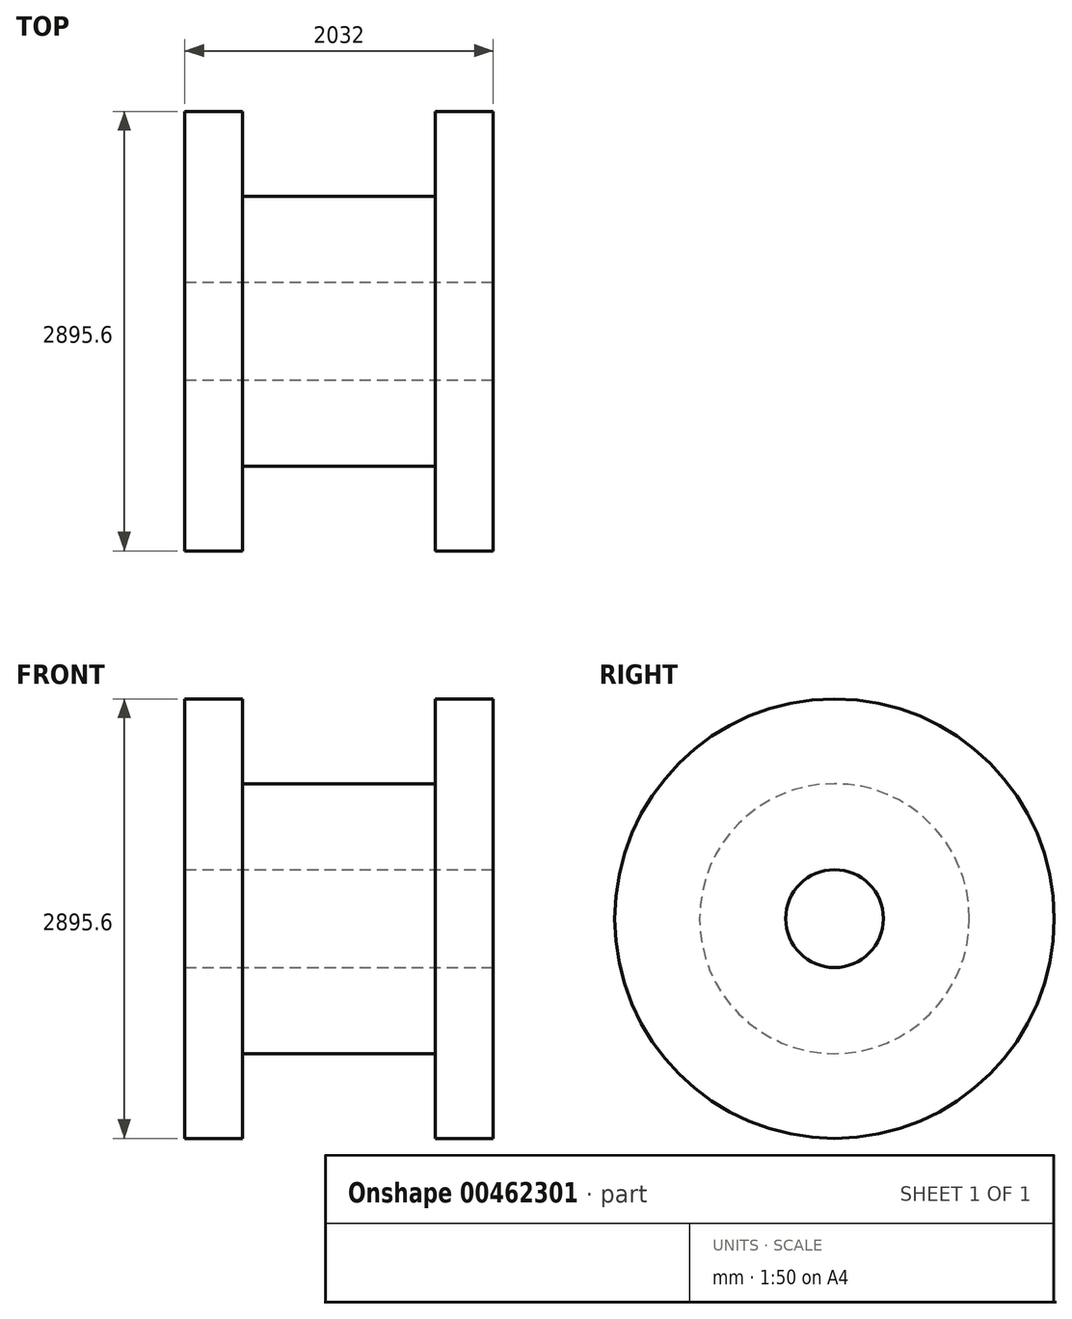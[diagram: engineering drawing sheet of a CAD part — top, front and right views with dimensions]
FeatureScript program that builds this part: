
annotation { "Feature Type Name" : "Feature", "Feature Type Description" : "" }
export const myFeature = defineFeature(function(context is Context, id is Id, definition is map)
    precondition{}
    {
        {
            var Q0;
            Q0=qCreatedBy(makeId("Front.planeOp"),FACE);
            var sketch = newSketch(context, id + "F0", { "sketchPlane" : qUnion([Q0])});
            skLineSegment(sketch, "E0.bottom", {"start": v(1016, 1618.8) * mm, "end": v(635, 1618.8) * mm});
            skLineSegment(sketch, "E0.top", {"start": v(1016, 171) * mm, "end": v(-1016, 171) * mm});
            skLineSegment(sketch, "E0.left", {"start": v(1016, 1618.8) * mm, "end": v(1016, 493.14) * mm});
            skLineSegment(sketch, "E0.right", {"start": v(-1016, 1618.8) * mm, "end": v(-1016, 493.14) * mm});
            skPoint(sketch, "E0.middle", {"position": v(0, 894.9) * mm});
            skLineSegment(sketch, "E1", {"start": v(-635, 1618.8) * mm, "end": v(-635, 1060) * mm});
            skLineSegment(sketch, "E2", {"start": v(-635, 1060) * mm, "end": v(635, 1060) * mm});
            skLineSegment(sketch, "E3", {"start": v(635, 1060) * mm, "end": v(635, 1618.8) * mm});
            skLineSegment(sketch, "E4.trimOffspring", {"start": v(-635, 1618.8) * mm, "end": v(-1016, 1618.8) * mm});
            skLineSegment(sketch, "E5", {"start": v(-1016, 493.14) * mm, "end": v(1016, 493.14) * mm});
            skSolve(sketch);
        }
        {
            var Q0;
            Q0 = qSketchRegion(id + "F0", true);
            var Q1;
            Q1=sQuery(id+"F0.wireOp",EDGE,"E0.top");
            revolve(context, id + "F1", {"entities" : qUnion([Q0]), "axis" : qUnion([Q1]), "revolveType" : RevolveType.FULL});
        }
    });
